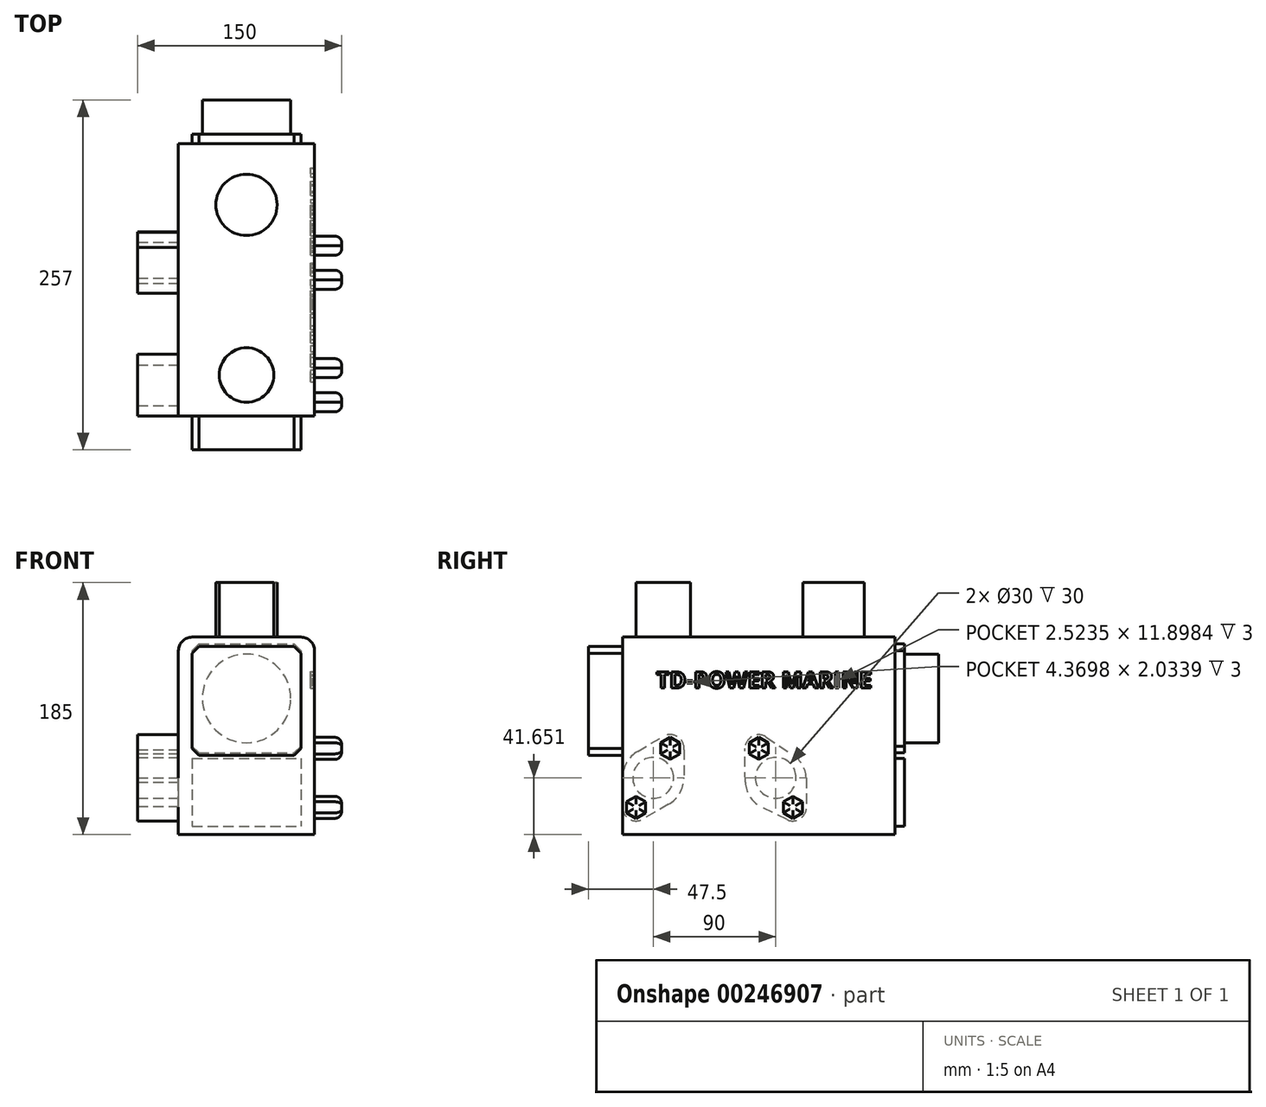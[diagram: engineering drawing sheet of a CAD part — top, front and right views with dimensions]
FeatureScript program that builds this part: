
annotation { "Feature Type Name" : "Feature", "Feature Type Description" : "" }
export const myFeature = defineFeature(function(context is Context, id is Id, definition is map)
    precondition{}
    {
        {
            var Q0;
            Q0=qCreatedBy(makeId("Right.planeOp"),FACE);
            var sketch = newSketch(context, id + "F0", { "sketchPlane" : qUnion([Q0])});
            skLineSegment(sketch, "E0.bottom", {"start": v(100, -72.5) * mm, "end": v(-100, -72.5) * mm});
            skLineSegment(sketch, "E0.top", {"start": v(100, 72.5) * mm, "end": v(-100, 72.5) * mm});
            skLineSegment(sketch, "E0.left", {"start": v(100, -72.5) * mm, "end": v(100, 72.5) * mm});
            skLineSegment(sketch, "E0.right", {"start": v(-100, -72.5) * mm, "end": v(-100, 72.5) * mm});
            skPoint(sketch, "E0.middle", {"position": v(0, 0) * mm});
            skSolve(sketch);
        }
        {
            var Q0;
            Q0 = qSketchRegion(id + "F0", true);
            extrude(context, id + "F1", {"entities" : qUnion([Q0]), "depth" : 100 * mm});
        }
        {
            var Q0;
            Q0=makeQuery(id+"F1.opExtrude","SWEPT_FACE",FACE,{"disambiguationData":[OSD([sQuery(id+"F0.wireOp",EDGE,"E0.top")])]});
            var sketch = newSketch(context, id + "F2", { "sketchPlane" : qUnion([Q0])});
            skCircle(sketch, "E1", {"center": v(50, -70) * mm, "radius": 20 * mm});
            skPoint(sketch, "E1.centerSnap0", {"position": v(50, -100) * mm});
            skCircle(sketch, "E2", {"center": v(50, 55) * mm, "radius": 22.5 * mm});
            skPoint(sketch, "E2.centerSnap0", {"position": v(50, 100) * mm});
            skSolve(sketch);
        }
        {
            var Q0;
            Q0 = qSketchRegion(id + "F2", true);
            extrude(context, id + "F3", {"entities" : qUnion([Q0]), "operationType" : NewBodyOperationType.ADD, "depth" : 40 * mm});
        }
        {
            var Q0;
            Q0=makeQuery(id+"F1.opExtrude","SWEPT_FACE",FACE,{"disambiguationData":[OSD([sQuery(id+"F0.wireOp",EDGE,"E0.left")])]});
            var sketch = newSketch(context, id + "F4", { "sketchPlane" : qUnion([Q0])});
            skLineSegment(sketch, "E3.bottom", {"start": v(-10, 67.47) * mm, "end": v(-90, 67.47) * mm});
            skLineSegment(sketch, "E3.top", {"start": v(-10, -12.53) * mm, "end": v(-90, -12.53) * mm});
            skLineSegment(sketch, "E3.left", {"start": v(-10, 67.47) * mm, "end": v(-10, -12.53) * mm});
            skLineSegment(sketch, "E3.right", {"start": v(-90, 67.47) * mm, "end": v(-90, -12.53) * mm});
            skPoint(sketch, "E3.middle", {"position": v(-50, 27.47) * mm});
            skPoint(sketch, "E3.middle.positionSnap0", {"position": v(-50, 72.5) * mm});
            skPoint(sketch, "E3.centerSnap0", {"position": v(-50, 72.5) * mm});
            skLineSegment(sketch, "E4.bottom", {"start": v(-10, -16.55) * mm, "end": v(-90, -16.55) * mm});
            skLineSegment(sketch, "E4.top", {"start": v(-10, -66.55) * mm, "end": v(-90, -66.55) * mm});
            skLineSegment(sketch, "E4.left", {"start": v(-10, -16.55) * mm, "end": v(-10, -66.55) * mm});
            skLineSegment(sketch, "E4.right", {"start": v(-90, -16.55) * mm, "end": v(-90, -66.55) * mm});
            skPoint(sketch, "E4.middle", {"position": v(-50, -41.55) * mm});
            skPoint(sketch, "E4.middle.positionSnap0", {"position": v(-50, -12.53) * mm});
            skPoint(sketch, "E4.centerSnap0", {"position": v(-50, -12.53) * mm});
            skSolve(sketch);
        }
        {
            var Q0;
            Q0 = qSketchRegion(id + "F4", true);
            extrude(context, id + "F5", {"entities" : qUnion([Q0]), "operationType" : NewBodyOperationType.ADD, "depth" : 7 * mm});
        }
        {
            var Q0;
            Q0=makeQuery(id+"F5.opExtrude","CAP_FACE",FACE,{"disambiguationData":[OSD([sQuery(id+"F4.wireOp",EDGE,"E3.bottom"),sQuery(id+"F4.wireOp",EDGE,"E3.top"),sQuery(id+"F4.wireOp",EDGE,"E3.left"),sQuery(id+"F4.wireOp",EDGE,"E3.right")])],"isStart":false});
            var sketch = newSketch(context, id + "F6", { "sketchPlane" : qUnion([Q0])});
            skCircle(sketch, "E5", {"center": v(-50, 27.47) * mm, "radius": 32.5 * mm});
            skPoint(sketch, "E5.centerSnap0", {"position": v(-10, 27.47) * mm});
            skPoint(sketch, "E5.centerSnap1", {"position": v(-50, 67.47) * mm});
            skSolve(sketch);
        }
        {
            var Q0;
            Q0 = qSketchRegion(id + "F6", true);
            extrude(context, id + "F7", {"entities" : qUnion([Q0]), "operationType" : NewBodyOperationType.ADD, "depth" : 25 * mm});
        }
        {
            var Q0;
            Q0=makeQuery(id+"F1.opExtrude","CAP_FACE",FACE,{"disambiguationData":[OSD([sQuery(id+"F0.wireOp",EDGE,"E0.bottom"),sQuery(id+"F0.wireOp",EDGE,"E0.top"),sQuery(id+"F0.wireOp",EDGE,"E0.left"),sQuery(id+"F0.wireOp",EDGE,"E0.right")])],"isStart":false});
            var sketch = newSketch(context, id + "F8", { "sketchPlane" : qUnion([Q0])});
            skText(sketch, "E6", { "text": "TD-POWER MARINE", "fontName": "OpenSans-Bold.ttf"});
            const initialGuessF8  = {"E6": [-0.0753, 0.03508, 1, 0, 0.012]};
            skSetInitialGuess(sketch, initialGuessF8);
            skSolve(sketch);
        }
        {
            var Q0;
            Q0 = qSketchRegion(id + "F8", true);
            extrude(context, id + "F9", {"entities" : qUnion([Q0]), "operationType" : NewBodyOperationType.REMOVE, "oppositeDirection" : true, "depth" : 3 * mm});
        }
        {
            var Q0;
            {var subQ0=sQuery(id+"F0.wireOp",EDGE,"E0.bottom");var subQ1=sQuery(id+"F0.wireOp",EDGE,"E0.right");var subQ2=sQuery(id+"F0.wireOp",EDGE,"E0.left");var subQ3=sQuery(id+"F0.wireOp",EDGE,"E0.top");Q0=makeQuery(id+"F9.boolean.opBoolean","SPLIT",FACE,{"disambiguationData":[TD([makeQuery(id+"F1.opExtrude","SWEPT_FACE",FACE,{"disambiguationData":[OSD([subQ0])]})])],"derivedFrom":makeQuery(id+"F1.opExtrude","CAP_FACE",FACE,{"disambiguationData":[OSD([subQ0,subQ3,subQ2,subQ1])],"isStart":false})});}
            var sketch = newSketch(context, id + "F10", { "sketchPlane" : qUnion([Q0])});
            skCircle(sketch, "E7.cCircle", {"center": v(-90, -52.5) * mm, "radius": 7 * mm, "construction": true});
            skLineSegment(sketch, "E7.0", {"start": v(-83, -48.46) * mm, "end": v(-83, -56.54) * mm});
            skLineSegment(sketch, "E7.1", {"start": v(-83, -56.54) * mm, "end": v(-90, -60.58) * mm});
            skLineSegment(sketch, "E7.2", {"start": v(-90, -60.58) * mm, "end": v(-97, -56.54) * mm});
            skLineSegment(sketch, "E7.3", {"start": v(-97, -56.54) * mm, "end": v(-97, -48.46) * mm});
            skLineSegment(sketch, "E7.4", {"start": v(-97, -48.46) * mm, "end": v(-90, -44.42) * mm});
            skLineSegment(sketch, "E7.5", {"start": v(-90, -44.42) * mm, "end": v(-83, -48.46) * mm});
            skPoint(sketch, "E7.0.midPoint", {"position": v(-83, -52.5) * mm});
            skCircle(sketch, "E8.cCircle", {"center": v(25, -52.5) * mm, "radius": 7 * mm, "construction": true});
            skLineSegment(sketch, "E8.0", {"start": v(32, -48.46) * mm, "end": v(32, -56.54) * mm});
            skLineSegment(sketch, "E8.1", {"start": v(32, -56.54) * mm, "end": v(25, -60.58) * mm});
            skLineSegment(sketch, "E8.2", {"start": v(25, -60.58) * mm, "end": v(18, -56.54) * mm});
            skLineSegment(sketch, "E8.3", {"start": v(18, -56.54) * mm, "end": v(18, -48.46) * mm});
            skLineSegment(sketch, "E8.4", {"start": v(18, -48.46) * mm, "end": v(25, -44.42) * mm});
            skLineSegment(sketch, "E8.5", {"start": v(25, -44.42) * mm, "end": v(32, -48.46) * mm});
            skPoint(sketch, "E8.0.midPoint", {"position": v(32, -52.5) * mm});
            skCircle(sketch, "E9.cCircle", {"center": v(-65, -9.2) * mm, "radius": 7 * mm, "construction": true});
            skLineSegment(sketch, "E9.0", {"start": v(-58, -13.24) * mm, "end": v(-65, -17.28) * mm});
            skLineSegment(sketch, "E9.1", {"start": v(-65, -17.28) * mm, "end": v(-72, -13.24) * mm});
            skLineSegment(sketch, "E9.2", {"start": v(-72, -13.24) * mm, "end": v(-72, -5.16) * mm});
            skLineSegment(sketch, "E9.3", {"start": v(-72, -5.16) * mm, "end": v(-65, -1.12) * mm});
            skLineSegment(sketch, "E9.4", {"start": v(-65, -1.12) * mm, "end": v(-58, -5.16) * mm});
            skLineSegment(sketch, "E9.5", {"start": v(-58, -5.16) * mm, "end": v(-58, -13.24) * mm});
            skPoint(sketch, "E9.0.midPoint", {"position": v(-61.5, -15.26) * mm});
            skCircle(sketch, "E10.cCircle", {"center": v(0, -9.2) * mm, "radius": 7 * mm, "construction": true});
            skPoint(sketch, "E10.cCircle.centerSnap0", {"position": v(-58, -9.2) * mm});
            skPoint(sketch, "E10.cCircle.perimeterSnap0", {"position": v(-58, -9.2) * mm});
            skLineSegment(sketch, "E10.0", {"start": v(7, -5.16) * mm, "end": v(7, -13.24) * mm});
            skLineSegment(sketch, "E10.1", {"start": v(7, -13.24) * mm, "end": v(0, -17.28) * mm});
            skLineSegment(sketch, "E10.2", {"start": v(0, -17.28) * mm, "end": v(-7, -13.24) * mm});
            skLineSegment(sketch, "E10.3", {"start": v(-7, -13.24) * mm, "end": v(-7, -5.16) * mm});
            skLineSegment(sketch, "E10.4", {"start": v(-7, -5.16) * mm, "end": v(0, -1.12) * mm});
            skLineSegment(sketch, "E10.5", {"start": v(0, -1.12) * mm, "end": v(7, -5.16) * mm});
            skPoint(sketch, "E10.0.midPoint", {"position": v(7, -9.2) * mm});
            skPoint(sketch, "E10.0.midPoint.positionSnap0", {"position": v(-58, -9.2) * mm});
            skLineSegment(sketch, "E11", {"start": v(-90, -52.5) * mm, "end": v(25, -52.5) * mm, "construction": true});
            skPoint(sketch, "E12.endSnap0", {"position": v(-32.5, -52.5) * mm});
            skLineSegment(sketch, "E13", {"start": v(-90, -52.5) * mm, "end": v(-65, -9.2) * mm, "construction": true});
            skLineSegment(sketch, "E14", {"start": v(25, -52.5) * mm, "end": v(0, -9.2) * mm, "construction": true});
            skSolve(sketch);
        }
        {
            var Q0;
            Q0 = qSketchRegion(id + "F10", true);
            extrude(context, id + "F11", {"entities" : qUnion([Q0]), "operationType" : NewBodyOperationType.ADD, "depth" : 20 * mm});
        }
        {
            var Q0;
            Q0=makeQuery(id+"F11.opExtrude","CAP_FACE",FACE,{"disambiguationData":[OSD([sQuery(id+"F10.wireOp",EDGE,"E7.0"),sQuery(id+"F10.wireOp",EDGE,"E7.1"),sQuery(id+"F10.wireOp",EDGE,"E7.2"),sQuery(id+"F10.wireOp",EDGE,"E7.3"),sQuery(id+"F10.wireOp",EDGE,"E7.4"),sQuery(id+"F10.wireOp",EDGE,"E7.5")])],"isStart":false});
            var Q1;
            Q1=makeQuery(id+"F11.opExtrude","CAP_FACE",FACE,{"disambiguationData":[OSD([sQuery(id+"F10.wireOp",EDGE,"E9.0"),sQuery(id+"F10.wireOp",EDGE,"E9.1"),sQuery(id+"F10.wireOp",EDGE,"E9.2"),sQuery(id+"F10.wireOp",EDGE,"E9.3"),sQuery(id+"F10.wireOp",EDGE,"E9.4"),sQuery(id+"F10.wireOp",EDGE,"E9.5")])],"isStart":false});
            var Q2;
            Q2=makeQuery(id+"F11.opExtrude","CAP_FACE",FACE,{"disambiguationData":[OSD([sQuery(id+"F10.wireOp",EDGE,"E10.0"),sQuery(id+"F10.wireOp",EDGE,"E10.1"),sQuery(id+"F10.wireOp",EDGE,"E10.2"),sQuery(id+"F10.wireOp",EDGE,"E10.3"),sQuery(id+"F10.wireOp",EDGE,"E10.4"),sQuery(id+"F10.wireOp",EDGE,"E10.5")])],"isStart":false});
            var Q3;
            Q3=makeQuery(id+"F11.opExtrude","CAP_FACE",FACE,{"disambiguationData":[OSD([sQuery(id+"F10.wireOp",EDGE,"E8.0"),sQuery(id+"F10.wireOp",EDGE,"E8.1"),sQuery(id+"F10.wireOp",EDGE,"E8.2"),sQuery(id+"F10.wireOp",EDGE,"E8.3"),sQuery(id+"F10.wireOp",EDGE,"E8.4"),sQuery(id+"F10.wireOp",EDGE,"E8.5")])],"isStart":false});
            fillet(context, id + "F12", {"entities" : qUnion([Q0, Q1, Q2, Q3]), "radius" : 5 * mm, "tangentPropagation" : true, "allowEdgeOverflow" : false});
        }
        {
            var Q0;
            Q0=makeQuery(id+"F1.opExtrude","SWEPT_FACE",FACE,{"disambiguationData":[OSD([sQuery(id+"F0.wireOp",EDGE,"E0.right")])]});
            var sketch = newSketch(context, id + "F13", { "sketchPlane" : qUnion([Q0])});
            skLineSegment(sketch, "E15.bottom", {"start": v(90, 65.65) * mm, "end": v(10, 65.65) * mm});
            skLineSegment(sketch, "E15.top", {"start": v(90, -14.35) * mm, "end": v(10, -14.35) * mm});
            skLineSegment(sketch, "E15.left", {"start": v(90, 65.65) * mm, "end": v(90, -14.35) * mm});
            skLineSegment(sketch, "E15.right", {"start": v(10, 65.65) * mm, "end": v(10, -14.35) * mm});
            skPoint(sketch, "E15.middle", {"position": v(50, 25.65) * mm});
            skPoint(sketch, "E15.middle.positionSnap0", {"position": v(50, 72.5) * mm});
            skPoint(sketch, "E15.centerSnap0", {"position": v(50, 72.5) * mm});
            skSolve(sketch);
        }
        {
            var Q0;
            Q0 = qSketchRegion(id + "F13", true);
            extrude(context, id + "F14", {"entities" : qUnion([Q0]), "operationType" : NewBodyOperationType.ADD, "depth" : 25 * mm});
        }
        {
            var Q0;
            Q0=makeQuery(id+"F14.opExtrude","SWEPT_EDGE",EDGE,{"disambiguationData":[OSD([sQuery(id+"F13.wireOp",EDGE,"E15.bottom"),sQuery(id+"F13.wireOp",EDGE,"E15.left")])]});
            var Q1;
            Q1=makeQuery(id+"F14.opExtrude","SWEPT_EDGE",EDGE,{"disambiguationData":[OSD([sQuery(id+"F13.wireOp",EDGE,"E15.top"),sQuery(id+"F13.wireOp",EDGE,"E15.left")])]});
            var Q2;
            Q2=makeQuery(id+"F14.opExtrude","SWEPT_EDGE",EDGE,{"disambiguationData":[OSD([sQuery(id+"F13.wireOp",EDGE,"E15.top"),sQuery(id+"F13.wireOp",EDGE,"E15.right")])]});
            var Q3;
            Q3=makeQuery(id+"F14.opExtrude","SWEPT_EDGE",EDGE,{"disambiguationData":[OSD([sQuery(id+"F13.wireOp",EDGE,"E15.bottom"),sQuery(id+"F13.wireOp",EDGE,"E15.right")])]});
            var Q4;
            Q4=makeQuery(id+"F5.opExtrude","SWEPT_EDGE",EDGE,{"disambiguationData":[OSD([sQuery(id+"F4.wireOp",EDGE,"E3.bottom"),sQuery(id+"F4.wireOp",EDGE,"E3.right")])]});
            var Q5;
            Q5=makeQuery(id+"F5.opExtrude","SWEPT_EDGE",EDGE,{"disambiguationData":[OSD([sQuery(id+"F4.wireOp",EDGE,"E3.bottom"),sQuery(id+"F4.wireOp",EDGE,"E3.left")])]});
            var Q6;
            Q6=makeQuery(id+"F5.opExtrude","SWEPT_EDGE",EDGE,{"disambiguationData":[OSD([sQuery(id+"F4.wireOp",EDGE,"E3.top"),sQuery(id+"F4.wireOp",EDGE,"E3.right")])]});
            var Q7;
            Q7=makeQuery(id+"F5.opExtrude","SWEPT_EDGE",EDGE,{"disambiguationData":[OSD([sQuery(id+"F4.wireOp",EDGE,"E3.top"),sQuery(id+"F4.wireOp",EDGE,"E3.left")])]});
            chamfer(context, id + "F15", {"entities" : qUnion([Q0, Q1, Q2, Q3, Q4, Q5, Q6, Q7]), "width" : 5 * mm, "tangentPropagation" : true});
        }
        {
            var Q0;
            Q0=makeQuery(id+"F1.opExtrude","CAP_EDGE",EDGE,{"disambiguationData":[OSD([sQuery(id+"F0.wireOp",EDGE,"E0.top")])],"isStart":false});
            var Q1;
            Q1=makeQuery(id+"F1.opExtrude","CAP_EDGE",EDGE,{"disambiguationData":[OSD([sQuery(id+"F0.wireOp",EDGE,"E0.top")])],"isStart":true});
            fillet(context, id + "F16", {"entities" : qUnion([Q0, Q1]), "radius" : 10 * mm, "tangentPropagation" : true, "allowEdgeOverflow" : false});
        }
        {
            var Q0;
            Q0=makeQuery(id+"F1.opExtrude","CAP_FACE",FACE,{"disambiguationData":[OSD([sQuery(id+"F0.wireOp",EDGE,"E0.bottom"),sQuery(id+"F0.wireOp",EDGE,"E0.top"),sQuery(id+"F0.wireOp",EDGE,"E0.left"),sQuery(id+"F0.wireOp",EDGE,"E0.right")])],"isStart":true});
            var sketch = newSketch(context, id + "F17", { "sketchPlane" : qUnion([Q0])});
            skPoint(sketch, "E16.0", {"position": v(0, -9.2) * mm});
            skPoint(sketch, "E16.1", {"position": v(65, -9.2) * mm});
            skPoint(sketch, "E16.2", {"position": v(90, -52.5) * mm});
            skPoint(sketch, "E16.3", {"position": v(-25, -52.5) * mm});
            skLineSegment(sketch, "E17", {"start": v(-25, -52.5) * mm, "end": v(0, -9.2) * mm, "construction": true});
            skLineSegment(sketch, "E18", {"start": v(90, -52.5) * mm, "end": v(65, -9.2) * mm, "construction": true});
            skCircle(sketch, "E19", {"center": v(-12.5, -30.85) * mm, "radius": 15 * mm});
            skCircle(sketch, "E20", {"center": v(77.5, -30.85) * mm, "radius": 15 * mm});
            skArc(sketch, "E21", {"start": v(55, -30.97) * mm, "mid": v(58.04, -42.15) * mm, "end": v(66.25, -50.33) * mm});
            skArc(sketch, "E22", {"start": v(10, -9.22) * mm, "mid": v(4.73, -0.39) * mm, "end": v(-5.55, -0.88) * mm});
            skArc(sketch, "E23", {"start": v(-35, -52.47) * mm, "mid": v(-30.3, -60.98) * mm, "end": v(-20.6, -61.48) * mm});
            skArc(sketch, "E24", {"start": v(85, -61.16) * mm, "mid": v(95, -61.16) * mm, "end": v(100, -52.5) * mm});
            skLineSegment(sketch, "E25", {"start": v(-5.55, -0.88) * mm, "end": v(-23.82, -13.05) * mm});
            skLineSegment(sketch, "E26", {"start": v(-34.94, -30.85) * mm, "end": v(-35, -52.47) * mm});
            skLineSegment(sketch, "E27", {"start": v(-20.6, -61.48) * mm, "end": v(-1.18, -51.95) * mm});
            skLineSegment(sketch, "E28", {"start": v(9.94, -34.15) * mm, "end": v(10, -9.22) * mm});
            skArc(sketch, "E29.trimOffspring", {"start": v(-1.18, -51.95) * mm, "mid": v(6.58, -44.42) * mm, "end": v(9.94, -34.15) * mm});
            skArc(sketch, "E30.trimOffspring", {"start": v(-23.82, -13.05) * mm, "mid": v(-31.58, -20.58) * mm, "end": v(-34.94, -30.85) * mm});
            skLineSegment(sketch, "E31", {"start": v(54.89, -10.1) * mm, "end": v(55, -30.97) * mm});
            skLineSegment(sketch, "E32", {"start": v(66.25, -50.33) * mm, "end": v(85, -61.16) * mm});
            skLineSegment(sketch, "E33", {"start": v(100, -52.5) * mm, "end": v(100, -30.85) * mm});
            skLineSegment(sketch, "E34", {"start": v(88.89, -11.44) * mm, "end": v(70.1, -0.42) * mm});
            skPoint(sketch, "E35.orphan", {"position": v(54.83, 0) * mm});
            skPoint(sketch, "E36.orphan", {"position": v(100, -69.82) * mm});
            skArc(sketch, "E37.trimOffspring", {"start": v(70.1, -0.42) * mm, "mid": v(59.55, -0.63) * mm, "end": v(54.89, -10.1) * mm});
            skArc(sketch, "E38.trimOffspring", {"start": v(100, -30.85) * mm, "mid": v(97.03, -19.67) * mm, "end": v(88.89, -11.44) * mm});
            skSolve(sketch);
        }
        {
            var Q0;
            Q0 = qSketchRegion(id + "F17", true);
            extrude(context, id + "F18", {"entities" : qUnion([Q0]), "operationType" : NewBodyOperationType.ADD, "depth" : 30 * mm});
        }
    });
